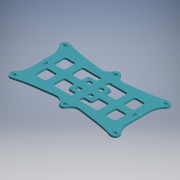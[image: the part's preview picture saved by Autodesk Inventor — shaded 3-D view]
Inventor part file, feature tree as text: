
AUTODESK INVENTOR PART (.ipt)
format: ipt  version: 2017 (Build 210142000, 142)  size: 440,320 bytes
history: native  units: mm (DEFAULTED — no unit token found)
features: extrude x6, sketch x6, fillet x5
ambient origin geometry x8: Origin, YZ Plane, XZ Plane, XY Plane, X Axis, Y Axis, Z Axis, Center Point
bodies: Solid1 (feature_tree)
feature tree (17):
  extrude  "Extrusion1"  Depth=24.0mm
  fillet  "Fillet3"  Radius=24.0mm
  fillet  "Fillet4"  Radius=24.0mm
  fillet  "Fillet5"  Radius=24.0mm
  fillet  "Fillet6"  Radius=24.0mm
  extrude  "Extrusion3"  Depth=24.0mm
  fillet  "Fillet7"  Radius=150.0mm
  extrude  "Extrusion4"  Depth=24.0mm
  extrude  "Extrusion6"  Depth=48.0mm
  extrude  "Extrusion7"  Depth=25.0mm
  extrude  "Extrusion8"  Depth=61.5mm
  sketch  "Sketch1"  dims[d6=5.0mm d7=0.0mm d27=24.0mm d28=24.0mm d30=24.0mm d32=24.0mm d34=24.0mm]
  sketch  "Sketch5"  dims[d36=24.0mm d40=150.0mm d42=150.0mm]
  sketch  "Sketch6"  dims[d43=12.0mm d44=24.0mm]
  sketch  "Sketch9"  dims[d45=360.0mm d46=48.0mm]
  sketch  "Sketch10"  dims[d47=25.0mm d48=30.0mm]
  sketch  "Sketch11"  dims[d49=70.0mm d50=61.5mm d51=10.0mm d52=10.0mm d53=20.0mm d54=20.0mm d55=20.0mm d56=20.0mm d57=10.0mm d58=0.0mm d59=5.0mm d60=7.5mm d61=10.0mm d62=0.0mm d65=2.75mm d66=29.0mm d67=24.5mm d77=7.0mm d78=7.0mm d79=2.0mm d80=7.0mm d81=7.0mm d82=7.0mm d83=7.0mm d84=7.0mm d85=7.0mm d86=7.0mm d87=7.0mm d88=7.0mm d89=7.0mm d90=10.0mm d91=0.0mm d92=4.0mm d93=1.0mm d94=0.0mm d98=1.0mm d99=0.0mm d100=5.0mm d101=10.0mm d102=10.0mm]
